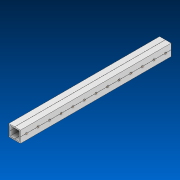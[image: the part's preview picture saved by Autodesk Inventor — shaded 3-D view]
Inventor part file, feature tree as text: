
AUTODESK INVENTOR PART (.ipt)
format: ipt  version: 2022.2 (Build 262287000, 287)  size: 681,984 bytes
history: native  units: in
note: dims shown in document units (in); Inventor stores cm internally (conversion verified against a paired STEP export)
features: other x13, extrude x1, pattern_linear x1, sketch x1, pattern_circular x1
ambient origin geometry x8: Origin, YZ Plane, XZ Plane, XY Plane, X Axis, Y Axis, Z Axis, Center Point
bodies: Solid1 (feature_tree)
feature tree (17):
  extrude  "Extrusion1"  Depth=1.0in
  other  "Work Axis1"
  pattern_linear  "Rectangular Pattern1"  Spacing1=0.0in  [1 undecoded]
  sketch  "Sketch1"  dims[d0=1.0in d1=46.0in d2=0.0in d3=5.1181in d5=1.0in]
  other  "Work Axis2"
  other  "Work Axis3"
  other  "Work Axis4"
  other  "Work Axis5"
  other  "Work Axis6"
  other  "Work Axis7"
  other  "Work Axis8"
  other  "Work Axis9"
  other  "Work Axis10"
  other  "Work Axis11"
  other  "Work Axis12"
  other  "Work Axis13"
  pattern_circular  "CirPattern2"
note: 1 required parameter value undecoded (feature->parameter linkage not recoverable at this tier; creation-order binding heuristic only, values carry confidence <= 0.55)
